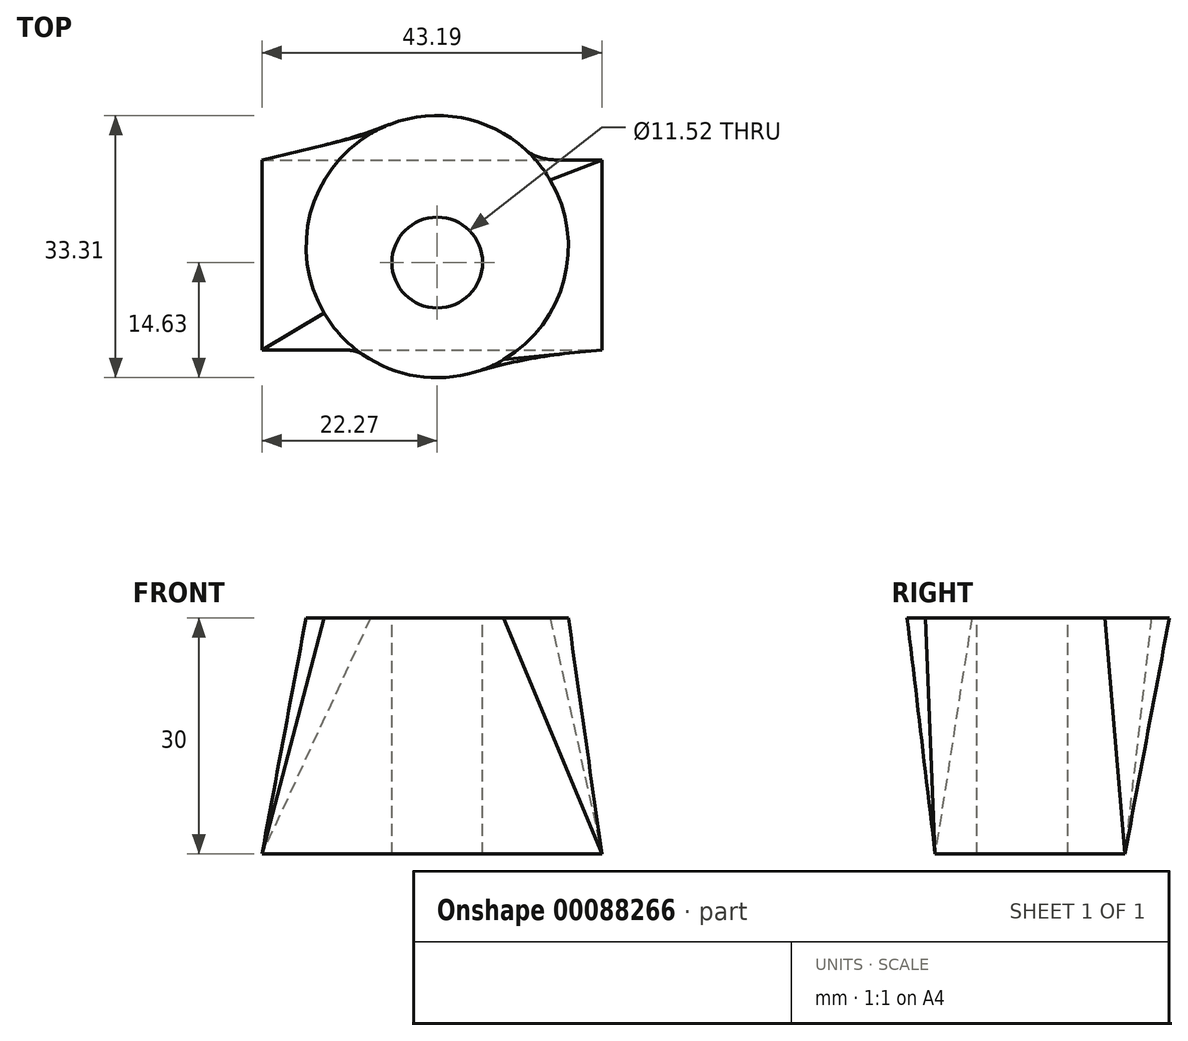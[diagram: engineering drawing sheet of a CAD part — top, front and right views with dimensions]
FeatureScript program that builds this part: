
annotation { "Feature Type Name" : "Feature", "Feature Type Description" : "" }
export const myFeature = defineFeature(function(context is Context, id is Id, definition is map)
    precondition{}
    {
        {
            var Q0;
            Q0=qCreatedBy(makeId("Top.planeOp"),FACE);
            var sketch = newSketch(context, id + "F0", { "sketchPlane" : qUnion([Q0])});
            skLineSegment(sketch, "E0.bottom", {"start": v(-22.27, -11.08) * mm, "end": v(20.92, -11.08) * mm});
            skLineSegment(sketch, "E0.top", {"start": v(-22.27, 13.01) * mm, "end": v(20.92, 13.01) * mm});
            skLineSegment(sketch, "E0.left", {"start": v(-22.27, -11.08) * mm, "end": v(-22.27, 13.01) * mm});
            skLineSegment(sketch, "E0.right", {"start": v(20.92, -11.08) * mm, "end": v(20.92, 13.01) * mm});
            skPoint(sketch, "E1", {"position": v(20.92, 13.01) * mm});
            skPoint(sketch, "E2", {"position": v(-22.27, 13.01) * mm});
            skPoint(sketch, "E3", {"position": v(-22.27, -11.08) * mm});
            skPoint(sketch, "E4", {"position": v(20.92, -11.08) * mm});
            skSolve(sketch);
        }
        {
            var Q0;
            Q0=qCreatedBy(makeId("Top.planeOp"),FACE);
            cPlane(context, id + "F1", {"entities" : qUnion([Q0]), "cplaneType" : CPlaneType.OFFSET, "offset" : 30 * mm, "width" : 150 * mm, "height" : 150 * mm});
        }
        {
            var Q0;
            Q0=qCreatedBy(id+"F1.planeOp",FACE);
            var sketch = newSketch(context, id + "F2", { "sketchPlane" : qUnion([Q0])});
            skCircle(sketch, "E5", {"center": v(0, 2.02) * mm, "radius": 16.66 * mm});
            skPoint(sketch, "E6", {"position": v(11.72, 13.85) * mm});
            skPoint(sketch, "E7", {"position": v(-12.01, 13.56) * mm});
            skPoint(sketch, "E8", {"position": v(-11.1, -10.4) * mm});
            skPoint(sketch, "E9", {"position": v(10.75, -10.7) * mm});
            skSolve(sketch);
        }
        {
            var Q0;
            Q0 = qSketchRegion(id + "F2", true);
            var Q1;
            Q1 = qSketchRegion(id + "F0", true);
            loft(context, id + "F3", {"sheetProfilesArray" : [{ "sheetProfileEntities" : qUnion([Q0]) }, { "sheetProfileEntities" : qUnion([Q1]) }]});
        }
        {
            var Q0;
            Q0=makeQuery(id+"F3.opLoft","CAP_FACE",FACE,{"disambiguationData":[OSD([makeQuery(id+"F2.imprint","IMPRINT",FACE,{"disambiguationData":[TD([[makeQuery(id+"F2.imprint","IMPRINT",EDGE,{"derivedFrom":sQuery(id+"F2.wireOp",EDGE,"E5")}),1.0]])]})])],"isStart":true});
            var sketch = newSketch(context, id + "F4", { "sketchPlane" : qUnion([Q0])});
            skCircle(sketch, "E10", {"center": v(0, 0) * mm, "radius": 5.76 * mm});
            skSolve(sketch);
        }
        {
            var Q0;
            Q0 = qSketchRegion(id + "F4", true);
            var Q1;
            Q1=sQuery(id+"F4.wireOp",EDGE,"E10");
            extrude(context, id + "F5", {"entities" : qUnion([Q0]), "operationType" : NewBodyOperationType.REMOVE, "surfaceEntities" : qUnion([Q1]), "oppositeDirection" : true, "depth" : 30 * mm});
        }
    });
